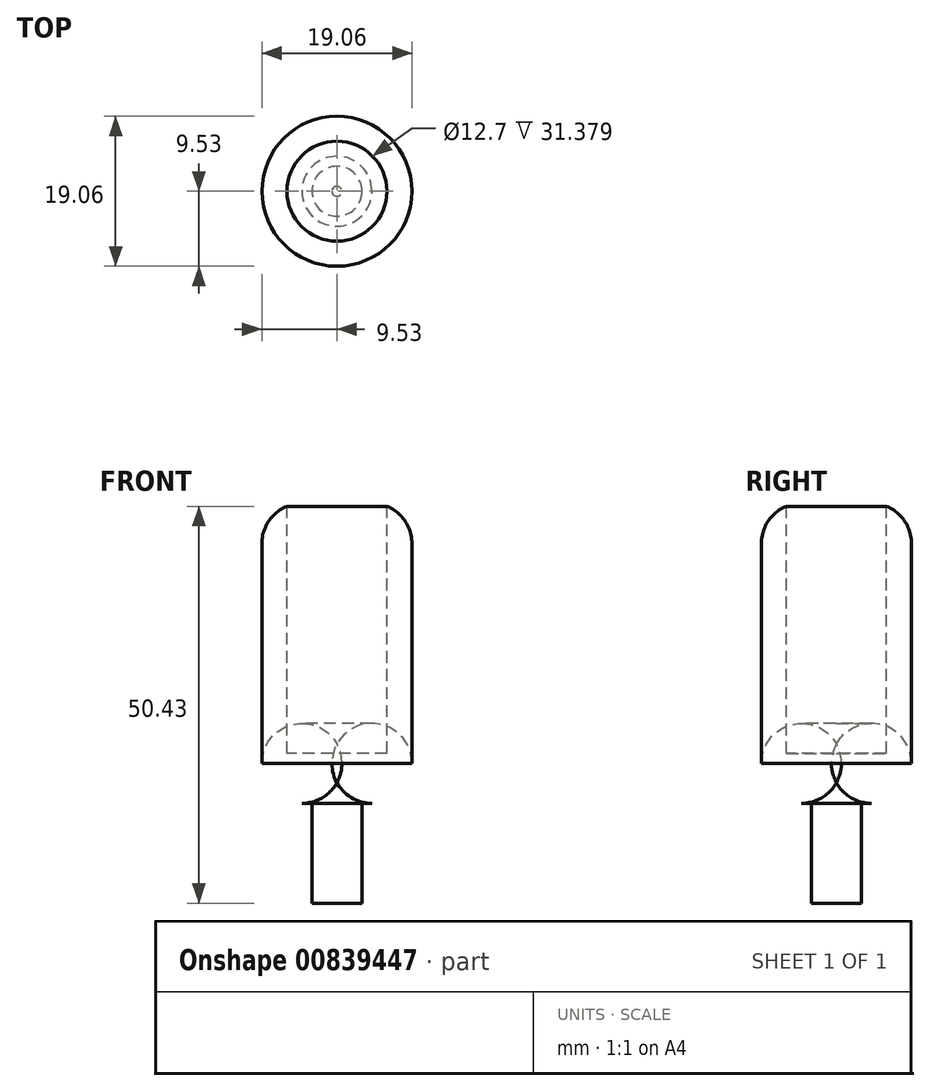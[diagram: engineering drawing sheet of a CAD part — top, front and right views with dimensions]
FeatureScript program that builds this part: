
annotation { "Feature Type Name" : "Feature", "Feature Type Description" : "" }
export const myFeature = defineFeature(function(context is Context, id is Id, definition is map)
    precondition{}
    {
        {
            var Q0;
            Q0=qCreatedBy(makeId("Top.planeOp"),FACE);
            var sketch = newSketch(context, id + "F0", { "sketchPlane" : qUnion([Q0])});
            skCircle(sketch, "E0", {"center": v(0, 0) * mm, "radius": 3.18 * mm});
            skSolve(sketch);
        }
        {
            var Q0;
            Q0 = qSketchRegion(id + "F0", true);
            extrude(context, id + "F1", {"entities" : qUnion([Q0]), "depth" : 12.7 * mm, "offsetDistance" : 25.4 * mm});
        }
        {
            var Q0;
            Q0=makeQuery(id+"F1.opExtrude","CAP_FACE",FACE,{"disambiguationData":[OSD([sQuery(id+"F0.wireOp",EDGE,"E0")])],"isStart":false});
            var sketch = newSketch(context, id + "F2", { "sketchPlane" : qUnion([Q0])});
            skCircle(sketch, "E1", {"center": v(0, 0) * mm, "radius": 9.53 * mm});
            skSolve(sketch);
        }
        {
            var Q0;
            Q0 = qSketchRegion(id + "F2", true);
            extrude(context, id + "F3", {"entities" : qUnion([Q0]), "operationType" : NewBodyOperationType.ADD, "depth" : 38.1 * mm, "offsetDistance" : 25.4 * mm});
        }
        {
            var Q0;
            Q0=makeQuery(id+"F3.opExtrude","CAP_EDGE",EDGE,{"disambiguationData":[OSD([sQuery(id+"F2.wireOp",EDGE,"E1")])],"isStart":false});
            var Q1;
            Q1=makeQuery(id+"F3.opExtrude","CAP_EDGE",EDGE,{"disambiguationData":[OSD([sQuery(id+"F2.wireOp",EDGE,"E1")])],"isStart":true});
            fillet(context, id + "F4", {"entities" : qUnion([Q0, Q1]), "tangentPropagation" : true, "radius" : 5.08 * mm, "defaultsChanged" : false, "vertexSettings" : [], "allowEdgeOverflow" : false});
        }
        {
            var Q0;
            Q0=makeQuery(id+"F3.opExtrude","CAP_FACE",FACE,{"disambiguationData":[OSD([sQuery(id+"F2.wireOp",EDGE,"E1")])],"isStart":false});
            var sketch = newSketch(context, id + "F5", { "sketchPlane" : qUnion([Q0])});
            skCircle(sketch, "E2", {"center": v(0, 0) * mm, "radius": 6.35 * mm});
            skSolve(sketch);
        }
        {
            var Q0;
            Q0 = qSketchRegion(id + "F5", true);
            extrude(context, id + "F6", {"entities" : qUnion([Q0]), "operationType" : NewBodyOperationType.REMOVE, "oppositeDirection" : true, "depth" : 31.75 * mm, "offsetDistance" : 25.4 * mm});
        }
    });
